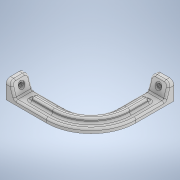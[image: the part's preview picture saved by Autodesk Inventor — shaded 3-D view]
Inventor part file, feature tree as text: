
AUTODESK INVENTOR PART (.ipt)
format: ipt  version: 2021 (Build 250183000, 183)  size: 302,080 bytes
history: native  units: mm
features: sketch x5, other x4, plane x2
ambient origin geometry x8: Origin, YZ Plane, XZ Plane, XY Plane, X Axis, Y Axis, Z Axis, Center Point
bodies: Body1 (feature_tree)
feature tree (11):
  other  "鋁擠加強肋(下層).ipt"
  other  "實體1::鋁擠加強肋(下層).ipt"
  other  "標籤特徵1"
  sketch  "草圖1"
  sketch  "草圖2"
  sketch  "草圖3"
  sketch  "草圖4"
  sketch  "草圖5"
  plane  "工作平面1"
  plane  "工作平面2"
  other  "實體1"
